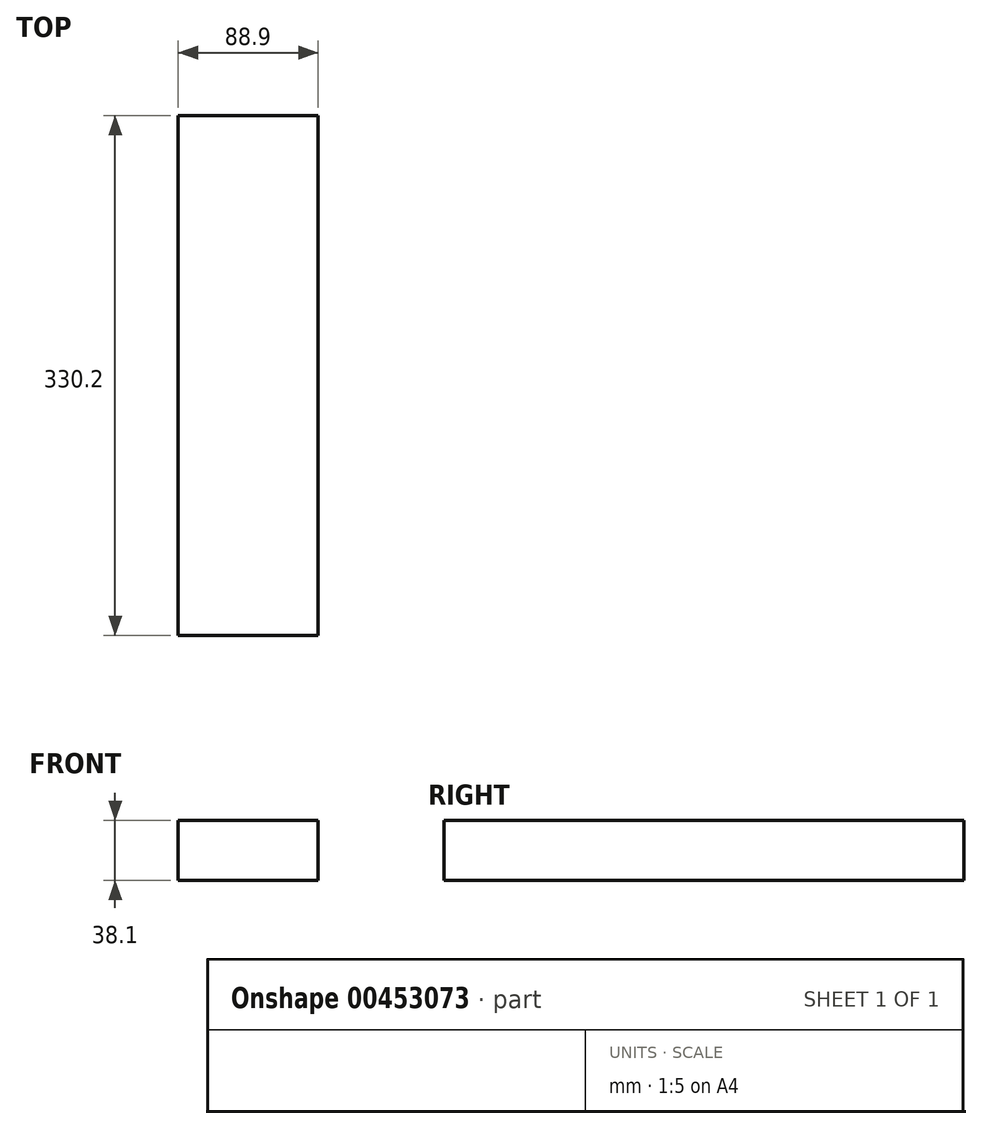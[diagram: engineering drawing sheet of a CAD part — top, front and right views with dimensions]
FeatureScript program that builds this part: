
annotation { "Feature Type Name" : "Feature", "Feature Type Description" : "" }
export const myFeature = defineFeature(function(context is Context, id is Id, definition is map)
    precondition{}
    {
        {
            var Q0;
            Q0=qCreatedBy(makeId("Front.planeOp"),FACE);
            var sketch = newSketch(context, id + "F0", { "sketchPlane" : qUnion([Q0])});
            skLineSegment(sketch, "E0.bottom", {"start": v(44.45, 19.05) * mm, "end": v(-44.45, 19.05) * mm});
            skLineSegment(sketch, "E0.top", {"start": v(44.45, -19.05) * mm, "end": v(-44.45, -19.05) * mm});
            skLineSegment(sketch, "E0.left", {"start": v(44.45, 19.05) * mm, "end": v(44.45, -19.05) * mm});
            skLineSegment(sketch, "E0.right", {"start": v(-44.45, 19.05) * mm, "end": v(-44.45, -19.05) * mm});
            skPoint(sketch, "E0.middle", {"position": v(0, 0) * mm});
            skSolve(sketch);
        }
        {
            var Q0;
            Q0 = qSketchRegion(id + "F0", true);
            extrude(context, id + "F1", {"entities" : qUnion([Q0]), "depth" : 330.2 * mm, "offsetDistance" : 25.4 * mm});
        }
    });
